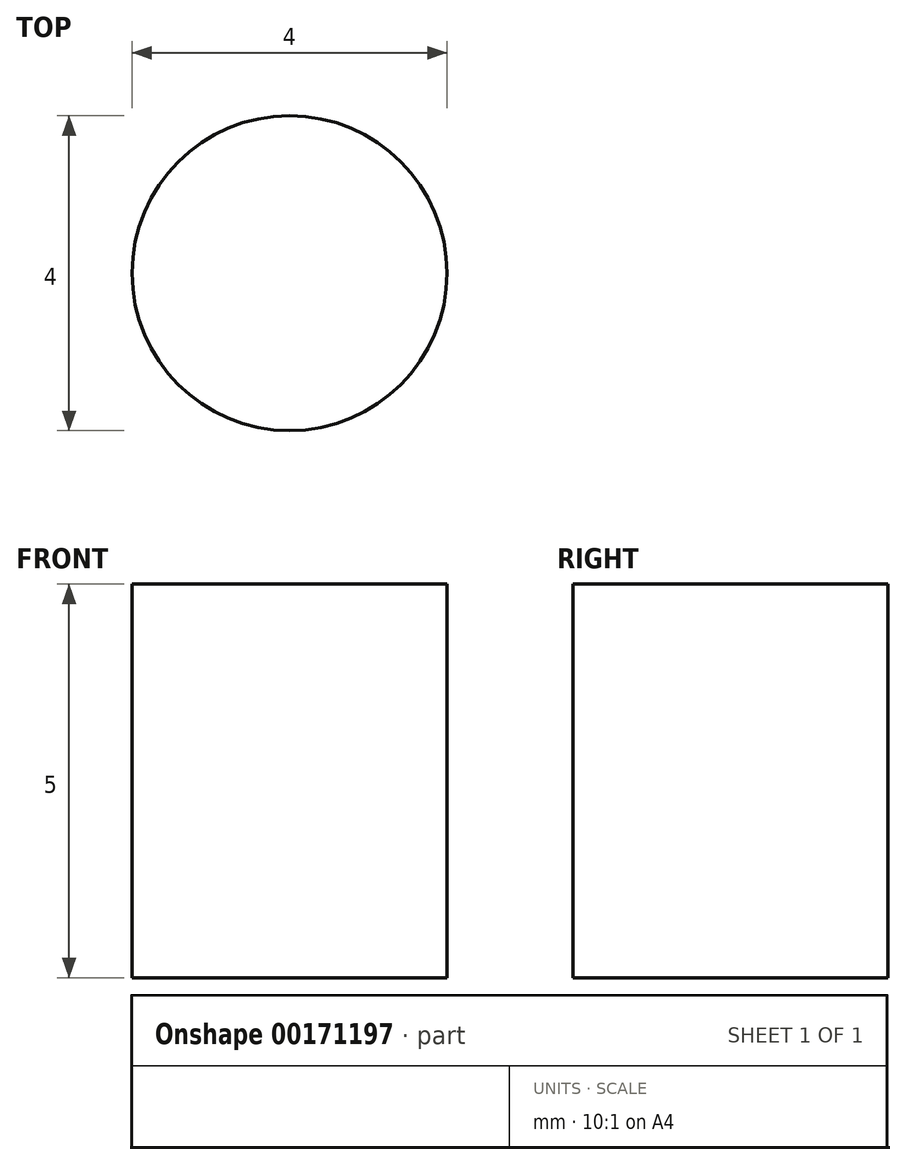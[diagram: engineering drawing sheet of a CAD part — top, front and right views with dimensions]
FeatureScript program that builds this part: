
annotation { "Feature Type Name" : "Feature", "Feature Type Description" : "" }
export const myFeature = defineFeature(function(context is Context, id is Id, definition is map)
    precondition{}
    {
        {
            var Q0;
            Q0=qCreatedBy(makeId("Top.planeOp"),FACE);
            var sketch = newSketch(context, id + "F0", { "sketchPlane" : qUnion([Q0])});
            skCircle(sketch, "E0", {"center": v(0, 0) * mm, "radius": 2 * mm});
            skLineSegment(sketch, "E1", {"start": v(5.33, 16.44) * mm, "end": v(4.24, 16.75) * mm});
            skArc(sketch, "E2", {"start": v(3.87, 17.95) * mm, "mid": v(3.86, 17.29) * mm, "end": v(4.24, 16.75) * mm});
            skArc(sketch, "E3", {"start": v(3.87, 17.95) * mm, "mid": v(3.9, 18.29) * mm, "end": v(3.9, 18.63) * mm});
            skLineSegment(sketch, "E4", {"start": v(3.9, 18.63) * mm, "end": v(3.86, 19) * mm});
            skArc(sketch, "E5", {"start": v(3.86, 19) * mm, "mid": v(3.65, 20.03) * mm, "end": v(3.31, 21.03) * mm});
            skLineSegment(sketch, "E6", {"start": v(3.31, 21.03) * mm, "end": v(3.26, 21.16) * mm});
            skLineSegment(sketch, "E7", {"start": v(3.26, 21.16) * mm, "end": v(2.02, 21.31) * mm});
            skLineSegment(sketch, "E8", {"start": v(2.02, 21.31) * mm, "end": v(1.93, 21.2) * mm});
            skArc(sketch, "E9", {"start": v(1.93, 21.2) * mm, "mid": v(1.37, 20.31) * mm, "end": v(0.91, 19.36) * mm});
            skLineSegment(sketch, "E10", {"start": v(0.91, 19.36) * mm, "end": v(0.79, 19.02) * mm});
            skArc(sketch, "E11", {"start": v(0.79, 19.02) * mm, "mid": v(0.69, 18.7) * mm, "end": v(0.64, 18.35) * mm});
            skArc(sketch, "E12", {"start": v(-0.01, 17.28) * mm, "mid": v(0.49, 17.7) * mm, "end": v(0.64, 18.35) * mm});
            skLineSegment(sketch, "E13", {"start": v(-0.01, 17.28) * mm, "end": v(-1.14, 17.24) * mm});
            skArc(sketch, "E14", {"start": v(-1.87, 18.27) * mm, "mid": v(-1.67, 17.64) * mm, "end": v(-1.14, 17.24) * mm});
            skArc(sketch, "E15", {"start": v(-1.87, 18.27) * mm, "mid": v(-1.93, 18.6) * mm, "end": v(-2.06, 18.92) * mm});
            skLineSegment(sketch, "E16", {"start": v(-2.06, 18.92) * mm, "end": v(-2.2, 19.26) * mm});
            skArc(sketch, "E17", {"start": v(-2.2, 19.26) * mm, "mid": v(-2.72, 20.18) * mm, "end": v(-3.35, 21.02) * mm});
            skLineSegment(sketch, "E18", {"start": v(-3.35, 21.02) * mm, "end": v(-3.44, 21.13) * mm});
            skLineSegment(sketch, "E19", {"start": v(-3.44, 21.13) * mm, "end": v(-4.67, 20.9) * mm});
            skLineSegment(sketch, "E20", {"start": v(-4.67, 20.9) * mm, "end": v(-4.71, 20.76) * mm});
            skArc(sketch, "E21", {"start": v(-4.71, 20.76) * mm, "mid": v(-4.98, 19.74) * mm, "end": v(-5.12, 18.7) * mm});
            skLineSegment(sketch, "E22", {"start": v(-5.12, 18.7) * mm, "end": v(-5.13, 18.33) * mm});
            skArc(sketch, "E23", {"start": v(-5.13, 18.33) * mm, "mid": v(-5.12, 17.99) * mm, "end": v(-5.06, 17.65) * mm});
            skArc(sketch, "E24", {"start": v(-5.35, 16.43) * mm, "mid": v(-5, 17) * mm, "end": v(-5.06, 17.65) * mm});
            skLineSegment(sketch, "E25", {"start": v(-5.35, 16.43) * mm, "end": v(-6.42, 16.04) * mm});
            skArc(sketch, "E26", {"start": v(-7.42, 16.8) * mm, "mid": v(-7.04, 16.26) * mm, "end": v(-6.42, 16.04) * mm});
            skArc(sketch, "E27", {"start": v(-7.42, 16.8) * mm, "mid": v(-7.59, 17.1) * mm, "end": v(-7.8, 17.36) * mm});
            skLineSegment(sketch, "E28", {"start": v(-7.8, 17.36) * mm, "end": v(-8.05, 17.64) * mm});
            skArc(sketch, "E29", {"start": v(-8.05, 17.64) * mm, "mid": v(-8.82, 18.35) * mm, "end": v(-9.68, 18.96) * mm});
            skLineSegment(sketch, "E30", {"start": v(-9.68, 18.96) * mm, "end": v(-9.8, 19.03) * mm});
            skLineSegment(sketch, "E31", {"start": v(-9.8, 19.03) * mm, "end": v(-10.9, 18.43) * mm});
            skLineSegment(sketch, "E32", {"start": v(-10.9, 18.43) * mm, "end": v(-10.9, 18.29) * mm});
            skArc(sketch, "E33", {"start": v(-10.9, 18.29) * mm, "mid": v(-10.83, 17.24) * mm, "end": v(-10.64, 16.2) * mm});
            skLineSegment(sketch, "E34", {"start": v(-10.64, 16.2) * mm, "end": v(-10.54, 15.85) * mm});
            skArc(sketch, "E35", {"start": v(-10.54, 15.85) * mm, "mid": v(-10.43, 15.52) * mm, "end": v(-10.27, 15.22) * mm});
            skArc(sketch, "E36", {"start": v(-10.16, 13.97) * mm, "mid": v(-10.01, 14.61) * mm, "end": v(-10.27, 15.22) * mm});
            skLineSegment(sketch, "E37", {"start": v(-10.16, 13.97) * mm, "end": v(-11.06, 13.27) * mm});
            skArc(sketch, "E38", {"start": v(-12.25, 13.68) * mm, "mid": v(-11.72, 13.28) * mm, "end": v(-11.06, 13.27) * mm});
            skArc(sketch, "E39", {"start": v(-12.25, 13.68) * mm, "mid": v(-12.5, 13.91) * mm, "end": v(-12.79, 14.1) * mm});
            skLineSegment(sketch, "E40", {"start": v(-12.79, 14.1) * mm, "end": v(-13.1, 14.29) * mm});
            skArc(sketch, "E41", {"start": v(-13.1, 14.29) * mm, "mid": v(-14.06, 14.72) * mm, "end": v(-15.06, 15.04) * mm});
            skLineSegment(sketch, "E42", {"start": v(-15.06, 15.04) * mm, "end": v(-15.2, 15.07) * mm});
            skLineSegment(sketch, "E43", {"start": v(-15.2, 15.07) * mm, "end": v(-16.06, 14.16) * mm});
            skLineSegment(sketch, "E44", {"start": v(-16.06, 14.16) * mm, "end": v(-16.01, 14.03) * mm});
            skArc(sketch, "E45", {"start": v(-16.01, 14.03) * mm, "mid": v(-15.63, 13.05) * mm, "end": v(-15.13, 12.12) * mm});
            skLineSegment(sketch, "E46", {"start": v(-15.13, 12.12) * mm, "end": v(-14.92, 11.82) * mm});
            skArc(sketch, "E47", {"start": v(-14.92, 11.82) * mm, "mid": v(-14.72, 11.54) * mm, "end": v(-14.47, 11.3) * mm});
            skArc(sketch, "E48", {"start": v(-13.98, 10.15) * mm, "mid": v(-14.04, 10.8) * mm, "end": v(-14.47, 11.3) * mm});
            skLineSegment(sketch, "E49", {"start": v(-13.98, 10.15) * mm, "end": v(-14.62, 9.2) * mm});
            skArc(sketch, "E50", {"start": v(-15.87, 9.23) * mm, "mid": v(-15.25, 9.01) * mm, "end": v(-14.62, 9.2) * mm});
            skArc(sketch, "E51", {"start": v(-15.87, 9.23) * mm, "mid": v(-16.19, 9.37) * mm, "end": v(-16.52, 9.46) * mm});
            skLineSegment(sketch, "E52", {"start": v(-16.52, 9.46) * mm, "end": v(-16.88, 9.54) * mm});
            skArc(sketch, "E53", {"start": v(-16.88, 9.54) * mm, "mid": v(-17.92, 9.66) * mm, "end": v(-18.97, 9.65) * mm});
            skLineSegment(sketch, "E54", {"start": v(-18.97, 9.65) * mm, "end": v(-19.12, 9.64) * mm});
            skLineSegment(sketch, "E55", {"start": v(-19.12, 9.64) * mm, "end": v(-19.65, 8.5) * mm});
            skLineSegment(sketch, "E56", {"start": v(-19.65, 8.5) * mm, "end": v(-19.56, 8.4) * mm});
            skArc(sketch, "E57", {"start": v(-19.56, 8.4) * mm, "mid": v(-18.9, 7.58) * mm, "end": v(-18.14, 6.85) * mm});
            skLineSegment(sketch, "E58", {"start": v(-18.14, 6.85) * mm, "end": v(-17.84, 6.63) * mm});
            skArc(sketch, "E59", {"start": v(-17.84, 6.63) * mm, "mid": v(-17.56, 6.43) * mm, "end": v(-17.25, 6.28) * mm});
            skArc(sketch, "E60", {"start": v(-16.44, 5.33) * mm, "mid": v(-16.69, 5.94) * mm, "end": v(-17.25, 6.28) * mm});
            skLineSegment(sketch, "E61", {"start": v(-16.44, 5.33) * mm, "end": v(-16.75, 4.24) * mm});
            skArc(sketch, "E62", {"start": v(-17.95, 3.87) * mm, "mid": v(-17.29, 3.86) * mm, "end": v(-16.75, 4.24) * mm});
            skArc(sketch, "E63", {"start": v(-17.95, 3.87) * mm, "mid": v(-18.29, 3.9) * mm, "end": v(-18.63, 3.9) * mm});
            skLineSegment(sketch, "E64", {"start": v(-18.63, 3.9) * mm, "end": v(-19, 3.86) * mm});
            skArc(sketch, "E65", {"start": v(-19, 3.86) * mm, "mid": v(-20.03, 3.65) * mm, "end": v(-21.03, 3.31) * mm});
            skLineSegment(sketch, "E66", {"start": v(-21.03, 3.31) * mm, "end": v(-21.16, 3.26) * mm});
            skLineSegment(sketch, "E67", {"start": v(-21.16, 3.26) * mm, "end": v(-21.31, 2.02) * mm});
            skLineSegment(sketch, "E68", {"start": v(-21.31, 2.02) * mm, "end": v(-21.2, 1.93) * mm});
            skArc(sketch, "E69", {"start": v(-21.2, 1.93) * mm, "mid": v(-20.31, 1.37) * mm, "end": v(-19.36, 0.91) * mm});
            skLineSegment(sketch, "E70", {"start": v(-19.36, 0.91) * mm, "end": v(-19.02, 0.79) * mm});
            skArc(sketch, "E71", {"start": v(-19.02, 0.79) * mm, "mid": v(-18.7, 0.69) * mm, "end": v(-18.35, 0.64) * mm});
            skArc(sketch, "E72", {"start": v(-17.28, -0.01) * mm, "mid": v(-17.7, 0.49) * mm, "end": v(-18.35, 0.64) * mm});
            skLineSegment(sketch, "E73", {"start": v(-17.28, -0.01) * mm, "end": v(-17.24, -1.14) * mm});
            skArc(sketch, "E74", {"start": v(-18.27, -1.87) * mm, "mid": v(-17.64, -1.67) * mm, "end": v(-17.24, -1.14) * mm});
            skArc(sketch, "E75", {"start": v(-18.27, -1.87) * mm, "mid": v(-18.6, -1.93) * mm, "end": v(-18.92, -2.06) * mm});
            skLineSegment(sketch, "E76", {"start": v(-18.92, -2.06) * mm, "end": v(-19.26, -2.2) * mm});
            skArc(sketch, "E77", {"start": v(-19.26, -2.2) * mm, "mid": v(-20.18, -2.72) * mm, "end": v(-21.02, -3.35) * mm});
            skLineSegment(sketch, "E78", {"start": v(-21.02, -3.35) * mm, "end": v(-21.13, -3.44) * mm});
            skLineSegment(sketch, "E79", {"start": v(-21.13, -3.44) * mm, "end": v(-20.9, -4.67) * mm});
            skLineSegment(sketch, "E80", {"start": v(-20.9, -4.67) * mm, "end": v(-20.76, -4.71) * mm});
            skArc(sketch, "E81", {"start": v(-20.76, -4.71) * mm, "mid": v(-19.74, -4.98) * mm, "end": v(-18.7, -5.12) * mm});
            skLineSegment(sketch, "E82", {"start": v(-18.7, -5.12) * mm, "end": v(-18.33, -5.13) * mm});
            skArc(sketch, "E83", {"start": v(-18.33, -5.13) * mm, "mid": v(-17.99, -5.12) * mm, "end": v(-17.65, -5.06) * mm});
            skArc(sketch, "E84", {"start": v(-16.43, -5.35) * mm, "mid": v(-17, -5) * mm, "end": v(-17.65, -5.06) * mm});
            skLineSegment(sketch, "E85", {"start": v(-16.43, -5.35) * mm, "end": v(-16.04, -6.42) * mm});
            skArc(sketch, "E86", {"start": v(-16.8, -7.42) * mm, "mid": v(-16.26, -7.04) * mm, "end": v(-16.04, -6.42) * mm});
            skArc(sketch, "E87", {"start": v(-16.8, -7.42) * mm, "mid": v(-17.1, -7.59) * mm, "end": v(-17.36, -7.8) * mm});
            skLineSegment(sketch, "E88", {"start": v(-17.36, -7.8) * mm, "end": v(-17.64, -8.05) * mm});
            skArc(sketch, "E89", {"start": v(-17.64, -8.05) * mm, "mid": v(-18.35, -8.82) * mm, "end": v(-18.96, -9.68) * mm});
            skLineSegment(sketch, "E90", {"start": v(-18.96, -9.68) * mm, "end": v(-19.03, -9.8) * mm});
            skLineSegment(sketch, "E91", {"start": v(-19.03, -9.8) * mm, "end": v(-18.43, -10.9) * mm});
            skLineSegment(sketch, "E92", {"start": v(-18.43, -10.9) * mm, "end": v(-18.29, -10.9) * mm});
            skArc(sketch, "E93", {"start": v(-18.29, -10.9) * mm, "mid": v(-17.24, -10.83) * mm, "end": v(-16.2, -10.64) * mm});
            skLineSegment(sketch, "E94", {"start": v(-16.2, -10.64) * mm, "end": v(-15.85, -10.54) * mm});
            skArc(sketch, "E95", {"start": v(-15.85, -10.54) * mm, "mid": v(-15.52, -10.43) * mm, "end": v(-15.22, -10.27) * mm});
            skArc(sketch, "E96", {"start": v(-13.97, -10.16) * mm, "mid": v(-14.61, -10.01) * mm, "end": v(-15.22, -10.27) * mm});
            skLineSegment(sketch, "E97", {"start": v(-13.97, -10.16) * mm, "end": v(-13.27, -11.06) * mm});
            skArc(sketch, "E98", {"start": v(-13.68, -12.25) * mm, "mid": v(-13.28, -11.72) * mm, "end": v(-13.27, -11.06) * mm});
            skArc(sketch, "E99", {"start": v(-13.68, -12.25) * mm, "mid": v(-13.91, -12.5) * mm, "end": v(-14.1, -12.79) * mm});
            skLineSegment(sketch, "E100", {"start": v(-14.1, -12.79) * mm, "end": v(-14.29, -13.1) * mm});
            skArc(sketch, "E101", {"start": v(-14.29, -13.1) * mm, "mid": v(-14.72, -14.06) * mm, "end": v(-15.04, -15.06) * mm});
            skLineSegment(sketch, "E102", {"start": v(-15.04, -15.06) * mm, "end": v(-15.07, -15.2) * mm});
            skLineSegment(sketch, "E103", {"start": v(-15.07, -15.2) * mm, "end": v(-14.16, -16.06) * mm});
            skLineSegment(sketch, "E104", {"start": v(-14.16, -16.06) * mm, "end": v(-14.03, -16.01) * mm});
            skArc(sketch, "E105", {"start": v(-14.03, -16.01) * mm, "mid": v(-13.05, -15.63) * mm, "end": v(-12.12, -15.13) * mm});
            skLineSegment(sketch, "E106", {"start": v(-12.12, -15.13) * mm, "end": v(-11.82, -14.92) * mm});
            skArc(sketch, "E107", {"start": v(-11.82, -14.92) * mm, "mid": v(-11.54, -14.72) * mm, "end": v(-11.3, -14.47) * mm});
            skArc(sketch, "E108", {"start": v(-10.15, -13.98) * mm, "mid": v(-10.8, -14.04) * mm, "end": v(-11.3, -14.47) * mm});
            skLineSegment(sketch, "E109", {"start": v(-10.15, -13.98) * mm, "end": v(-9.2, -14.62) * mm});
            skArc(sketch, "E110", {"start": v(-9.23, -15.87) * mm, "mid": v(-9.01, -15.25) * mm, "end": v(-9.2, -14.62) * mm});
            skArc(sketch, "E111", {"start": v(-9.23, -15.87) * mm, "mid": v(-9.37, -16.19) * mm, "end": v(-9.46, -16.52) * mm});
            skLineSegment(sketch, "E112", {"start": v(-9.46, -16.52) * mm, "end": v(-9.54, -16.88) * mm});
            skArc(sketch, "E113", {"start": v(-9.54, -16.88) * mm, "mid": v(-9.66, -17.92) * mm, "end": v(-9.65, -18.97) * mm});
            skLineSegment(sketch, "E114", {"start": v(-9.65, -18.97) * mm, "end": v(-9.64, -19.12) * mm});
            skLineSegment(sketch, "E115", {"start": v(-9.64, -19.12) * mm, "end": v(-8.5, -19.65) * mm});
            skLineSegment(sketch, "E116", {"start": v(-8.5, -19.65) * mm, "end": v(-8.4, -19.56) * mm});
            skArc(sketch, "E117", {"start": v(-8.4, -19.56) * mm, "mid": v(-7.58, -18.9) * mm, "end": v(-6.85, -18.14) * mm});
            skLineSegment(sketch, "E118", {"start": v(-6.85, -18.14) * mm, "end": v(-6.63, -17.84) * mm});
            skArc(sketch, "E119", {"start": v(-6.63, -17.84) * mm, "mid": v(-6.43, -17.56) * mm, "end": v(-6.28, -17.25) * mm});
            skArc(sketch, "E120", {"start": v(-5.33, -16.44) * mm, "mid": v(-5.94, -16.69) * mm, "end": v(-6.28, -17.25) * mm});
            skLineSegment(sketch, "E121", {"start": v(-5.33, -16.44) * mm, "end": v(-4.24, -16.75) * mm});
            skArc(sketch, "E122", {"start": v(-3.87, -17.95) * mm, "mid": v(-3.86, -17.29) * mm, "end": v(-4.24, -16.75) * mm});
            skArc(sketch, "E123", {"start": v(-3.87, -17.95) * mm, "mid": v(-3.9, -18.29) * mm, "end": v(-3.9, -18.63) * mm});
            skLineSegment(sketch, "E124", {"start": v(-3.9, -18.63) * mm, "end": v(-3.86, -19) * mm});
            skArc(sketch, "E125", {"start": v(-3.86, -19) * mm, "mid": v(-3.65, -20.03) * mm, "end": v(-3.31, -21.03) * mm});
            skLineSegment(sketch, "E126", {"start": v(-3.31, -21.03) * mm, "end": v(-3.26, -21.16) * mm});
            skLineSegment(sketch, "E127", {"start": v(-3.26, -21.16) * mm, "end": v(-2.02, -21.31) * mm});
            skLineSegment(sketch, "E128", {"start": v(-2.02, -21.31) * mm, "end": v(-1.93, -21.2) * mm});
            skArc(sketch, "E129", {"start": v(-1.93, -21.2) * mm, "mid": v(-1.37, -20.31) * mm, "end": v(-0.91, -19.36) * mm});
            skLineSegment(sketch, "E130", {"start": v(-0.91, -19.36) * mm, "end": v(-0.79, -19.02) * mm});
            skArc(sketch, "E131", {"start": v(-0.79, -19.02) * mm, "mid": v(-0.69, -18.7) * mm, "end": v(-0.64, -18.35) * mm});
            skArc(sketch, "E132", {"start": v(0.01, -17.28) * mm, "mid": v(-0.49, -17.7) * mm, "end": v(-0.64, -18.35) * mm});
            skLineSegment(sketch, "E133", {"start": v(0.01, -17.28) * mm, "end": v(1.14, -17.24) * mm});
            skArc(sketch, "E134", {"start": v(1.87, -18.27) * mm, "mid": v(1.67, -17.64) * mm, "end": v(1.14, -17.24) * mm});
            skArc(sketch, "E135", {"start": v(1.87, -18.27) * mm, "mid": v(1.93, -18.6) * mm, "end": v(2.06, -18.92) * mm});
            skLineSegment(sketch, "E136", {"start": v(2.06, -18.92) * mm, "end": v(2.2, -19.26) * mm});
            skArc(sketch, "E137", {"start": v(2.2, -19.26) * mm, "mid": v(2.72, -20.18) * mm, "end": v(3.35, -21.02) * mm});
            skLineSegment(sketch, "E138", {"start": v(3.35, -21.02) * mm, "end": v(3.44, -21.13) * mm});
            skLineSegment(sketch, "E139", {"start": v(3.44, -21.13) * mm, "end": v(4.67, -20.9) * mm});
            skLineSegment(sketch, "E140", {"start": v(4.67, -20.9) * mm, "end": v(4.71, -20.76) * mm});
            skArc(sketch, "E141", {"start": v(4.71, -20.76) * mm, "mid": v(4.98, -19.74) * mm, "end": v(5.12, -18.7) * mm});
            skLineSegment(sketch, "E142", {"start": v(5.12, -18.7) * mm, "end": v(5.13, -18.33) * mm});
            skArc(sketch, "E143", {"start": v(5.13, -18.33) * mm, "mid": v(5.12, -17.99) * mm, "end": v(5.06, -17.65) * mm});
            skArc(sketch, "E144", {"start": v(5.35, -16.43) * mm, "mid": v(5, -17) * mm, "end": v(5.06, -17.65) * mm});
            skLineSegment(sketch, "E145", {"start": v(5.35, -16.43) * mm, "end": v(6.42, -16.04) * mm});
            skArc(sketch, "E146", {"start": v(7.42, -16.8) * mm, "mid": v(7.04, -16.26) * mm, "end": v(6.42, -16.04) * mm});
            skArc(sketch, "E147", {"start": v(7.42, -16.8) * mm, "mid": v(7.59, -17.1) * mm, "end": v(7.8, -17.36) * mm});
            skLineSegment(sketch, "E148", {"start": v(7.8, -17.36) * mm, "end": v(8.05, -17.64) * mm});
            skArc(sketch, "E149", {"start": v(8.05, -17.64) * mm, "mid": v(8.82, -18.35) * mm, "end": v(9.68, -18.96) * mm});
            skLineSegment(sketch, "E150", {"start": v(9.68, -18.96) * mm, "end": v(9.8, -19.03) * mm});
            skLineSegment(sketch, "E151", {"start": v(9.8, -19.03) * mm, "end": v(10.9, -18.43) * mm});
            skLineSegment(sketch, "E152", {"start": v(10.9, -18.43) * mm, "end": v(10.9, -18.29) * mm});
            skArc(sketch, "E153", {"start": v(10.9, -18.29) * mm, "mid": v(10.83, -17.24) * mm, "end": v(10.64, -16.2) * mm});
            skLineSegment(sketch, "E154", {"start": v(10.64, -16.2) * mm, "end": v(10.54, -15.85) * mm});
            skArc(sketch, "E155", {"start": v(10.54, -15.85) * mm, "mid": v(10.43, -15.52) * mm, "end": v(10.27, -15.22) * mm});
            skArc(sketch, "E156", {"start": v(10.16, -13.97) * mm, "mid": v(10.01, -14.61) * mm, "end": v(10.27, -15.22) * mm});
            skLineSegment(sketch, "E157", {"start": v(10.16, -13.97) * mm, "end": v(11.06, -13.27) * mm});
            skArc(sketch, "E158", {"start": v(12.25, -13.68) * mm, "mid": v(11.72, -13.28) * mm, "end": v(11.06, -13.27) * mm});
            skArc(sketch, "E159", {"start": v(12.25, -13.68) * mm, "mid": v(12.5, -13.91) * mm, "end": v(12.79, -14.1) * mm});
            skLineSegment(sketch, "E160", {"start": v(12.79, -14.1) * mm, "end": v(13.1, -14.29) * mm});
            skArc(sketch, "E161", {"start": v(13.1, -14.29) * mm, "mid": v(14.06, -14.72) * mm, "end": v(15.06, -15.04) * mm});
            skLineSegment(sketch, "E162", {"start": v(15.06, -15.04) * mm, "end": v(15.2, -15.07) * mm});
            skLineSegment(sketch, "E163", {"start": v(15.2, -15.07) * mm, "end": v(16.06, -14.16) * mm});
            skLineSegment(sketch, "E164", {"start": v(16.06, -14.16) * mm, "end": v(16.01, -14.03) * mm});
            skArc(sketch, "E165", {"start": v(16.01, -14.03) * mm, "mid": v(15.63, -13.05) * mm, "end": v(15.13, -12.12) * mm});
            skLineSegment(sketch, "E166", {"start": v(15.13, -12.12) * mm, "end": v(14.92, -11.82) * mm});
            skArc(sketch, "E167", {"start": v(14.92, -11.82) * mm, "mid": v(14.72, -11.54) * mm, "end": v(14.47, -11.3) * mm});
            skArc(sketch, "E168", {"start": v(13.98, -10.15) * mm, "mid": v(14.04, -10.8) * mm, "end": v(14.47, -11.3) * mm});
            skLineSegment(sketch, "E169", {"start": v(13.98, -10.15) * mm, "end": v(14.62, -9.2) * mm});
            skArc(sketch, "E170", {"start": v(15.87, -9.23) * mm, "mid": v(15.25, -9.01) * mm, "end": v(14.62, -9.2) * mm});
            skArc(sketch, "E171", {"start": v(15.87, -9.23) * mm, "mid": v(16.19, -9.37) * mm, "end": v(16.52, -9.46) * mm});
            skLineSegment(sketch, "E172", {"start": v(16.52, -9.46) * mm, "end": v(16.88, -9.54) * mm});
            skArc(sketch, "E173", {"start": v(16.88, -9.54) * mm, "mid": v(17.92, -9.66) * mm, "end": v(18.97, -9.65) * mm});
            skLineSegment(sketch, "E174", {"start": v(18.97, -9.65) * mm, "end": v(19.12, -9.64) * mm});
            skLineSegment(sketch, "E175", {"start": v(19.12, -9.64) * mm, "end": v(19.65, -8.5) * mm});
            skLineSegment(sketch, "E176", {"start": v(19.65, -8.5) * mm, "end": v(19.56, -8.4) * mm});
            skArc(sketch, "E177", {"start": v(19.56, -8.4) * mm, "mid": v(18.9, -7.58) * mm, "end": v(18.14, -6.85) * mm});
            skLineSegment(sketch, "E178", {"start": v(18.14, -6.85) * mm, "end": v(17.84, -6.63) * mm});
            skArc(sketch, "E179", {"start": v(17.84, -6.63) * mm, "mid": v(17.56, -6.43) * mm, "end": v(17.25, -6.28) * mm});
            skArc(sketch, "E180", {"start": v(16.44, -5.33) * mm, "mid": v(16.69, -5.94) * mm, "end": v(17.25, -6.28) * mm});
            skLineSegment(sketch, "E181", {"start": v(16.44, -5.33) * mm, "end": v(16.75, -4.24) * mm});
            skArc(sketch, "E182", {"start": v(17.95, -3.87) * mm, "mid": v(17.29, -3.86) * mm, "end": v(16.75, -4.24) * mm});
            skArc(sketch, "E183", {"start": v(17.95, -3.87) * mm, "mid": v(18.29, -3.9) * mm, "end": v(18.63, -3.9) * mm});
            skLineSegment(sketch, "E184", {"start": v(18.63, -3.9) * mm, "end": v(19, -3.86) * mm});
            skArc(sketch, "E185", {"start": v(19, -3.86) * mm, "mid": v(20.03, -3.65) * mm, "end": v(21.03, -3.31) * mm});
            skLineSegment(sketch, "E186", {"start": v(21.03, -3.31) * mm, "end": v(21.16, -3.26) * mm});
            skLineSegment(sketch, "E187", {"start": v(21.16, -3.26) * mm, "end": v(21.31, -2.02) * mm});
            skLineSegment(sketch, "E188", {"start": v(21.31, -2.02) * mm, "end": v(21.2, -1.93) * mm});
            skArc(sketch, "E189", {"start": v(21.2, -1.93) * mm, "mid": v(20.31, -1.37) * mm, "end": v(19.36, -0.91) * mm});
            skLineSegment(sketch, "E190", {"start": v(19.36, -0.91) * mm, "end": v(19.02, -0.79) * mm});
            skArc(sketch, "E191", {"start": v(19.02, -0.79) * mm, "mid": v(18.7, -0.69) * mm, "end": v(18.35, -0.64) * mm});
            skArc(sketch, "E192", {"start": v(17.28, 0.01) * mm, "mid": v(17.7, -0.49) * mm, "end": v(18.35, -0.64) * mm});
            skLineSegment(sketch, "E193", {"start": v(17.28, 0.01) * mm, "end": v(17.24, 1.14) * mm});
            skArc(sketch, "E194", {"start": v(18.27, 1.87) * mm, "mid": v(17.64, 1.67) * mm, "end": v(17.24, 1.14) * mm});
            skArc(sketch, "E195", {"start": v(18.27, 1.87) * mm, "mid": v(18.6, 1.93) * mm, "end": v(18.92, 2.06) * mm});
            skLineSegment(sketch, "E196", {"start": v(18.92, 2.06) * mm, "end": v(19.26, 2.2) * mm});
            skArc(sketch, "E197", {"start": v(19.26, 2.2) * mm, "mid": v(20.18, 2.72) * mm, "end": v(21.02, 3.35) * mm});
            skLineSegment(sketch, "E198", {"start": v(21.02, 3.35) * mm, "end": v(21.13, 3.44) * mm});
            skLineSegment(sketch, "E199", {"start": v(21.13, 3.44) * mm, "end": v(20.9, 4.67) * mm});
            skLineSegment(sketch, "E200", {"start": v(20.9, 4.67) * mm, "end": v(20.76, 4.71) * mm});
            skArc(sketch, "E201", {"start": v(20.76, 4.71) * mm, "mid": v(19.74, 4.98) * mm, "end": v(18.7, 5.12) * mm});
            skLineSegment(sketch, "E202", {"start": v(18.7, 5.12) * mm, "end": v(18.33, 5.13) * mm});
            skArc(sketch, "E203", {"start": v(18.33, 5.13) * mm, "mid": v(17.99, 5.12) * mm, "end": v(17.65, 5.06) * mm});
            skArc(sketch, "E204", {"start": v(16.43, 5.35) * mm, "mid": v(17, 5) * mm, "end": v(17.65, 5.06) * mm});
            skLineSegment(sketch, "E205", {"start": v(16.43, 5.35) * mm, "end": v(16.04, 6.42) * mm});
            skArc(sketch, "E206", {"start": v(16.8, 7.42) * mm, "mid": v(16.26, 7.04) * mm, "end": v(16.04, 6.42) * mm});
            skArc(sketch, "E207", {"start": v(16.8, 7.42) * mm, "mid": v(17.1, 7.59) * mm, "end": v(17.36, 7.8) * mm});
            skLineSegment(sketch, "E208", {"start": v(17.36, 7.8) * mm, "end": v(17.64, 8.05) * mm});
            skArc(sketch, "E209", {"start": v(17.64, 8.05) * mm, "mid": v(18.35, 8.82) * mm, "end": v(18.96, 9.68) * mm});
            skLineSegment(sketch, "E210", {"start": v(18.96, 9.68) * mm, "end": v(19.03, 9.8) * mm});
            skLineSegment(sketch, "E211", {"start": v(19.03, 9.8) * mm, "end": v(18.43, 10.9) * mm});
            skLineSegment(sketch, "E212", {"start": v(18.43, 10.9) * mm, "end": v(18.29, 10.9) * mm});
            skArc(sketch, "E213", {"start": v(18.29, 10.9) * mm, "mid": v(17.24, 10.83) * mm, "end": v(16.2, 10.64) * mm});
            skLineSegment(sketch, "E214", {"start": v(16.2, 10.64) * mm, "end": v(15.85, 10.54) * mm});
            skArc(sketch, "E215", {"start": v(15.85, 10.54) * mm, "mid": v(15.52, 10.43) * mm, "end": v(15.22, 10.27) * mm});
            skArc(sketch, "E216", {"start": v(13.97, 10.16) * mm, "mid": v(14.61, 10.01) * mm, "end": v(15.22, 10.27) * mm});
            skLineSegment(sketch, "E217", {"start": v(13.97, 10.16) * mm, "end": v(13.27, 11.06) * mm});
            skArc(sketch, "E218", {"start": v(13.68, 12.25) * mm, "mid": v(13.28, 11.72) * mm, "end": v(13.27, 11.06) * mm});
            skArc(sketch, "E219", {"start": v(13.68, 12.25) * mm, "mid": v(13.91, 12.5) * mm, "end": v(14.1, 12.79) * mm});
            skLineSegment(sketch, "E220", {"start": v(14.1, 12.79) * mm, "end": v(14.29, 13.1) * mm});
            skArc(sketch, "E221", {"start": v(14.29, 13.1) * mm, "mid": v(14.72, 14.06) * mm, "end": v(15.04, 15.06) * mm});
            skLineSegment(sketch, "E222", {"start": v(15.04, 15.06) * mm, "end": v(15.07, 15.2) * mm});
            skLineSegment(sketch, "E223", {"start": v(15.07, 15.2) * mm, "end": v(14.16, 16.06) * mm});
            skLineSegment(sketch, "E224", {"start": v(14.16, 16.06) * mm, "end": v(14.03, 16.01) * mm});
            skArc(sketch, "E225", {"start": v(14.03, 16.01) * mm, "mid": v(13.05, 15.63) * mm, "end": v(12.12, 15.13) * mm});
            skLineSegment(sketch, "E226", {"start": v(12.12, 15.13) * mm, "end": v(11.82, 14.92) * mm});
            skArc(sketch, "E227", {"start": v(11.82, 14.92) * mm, "mid": v(11.54, 14.72) * mm, "end": v(11.3, 14.47) * mm});
            skArc(sketch, "E228", {"start": v(10.15, 13.98) * mm, "mid": v(10.8, 14.04) * mm, "end": v(11.3, 14.47) * mm});
            skLineSegment(sketch, "E229", {"start": v(10.15, 13.98) * mm, "end": v(9.2, 14.62) * mm});
            skArc(sketch, "E230", {"start": v(9.23, 15.87) * mm, "mid": v(9.01, 15.25) * mm, "end": v(9.2, 14.62) * mm});
            skArc(sketch, "E231", {"start": v(9.23, 15.87) * mm, "mid": v(9.37, 16.19) * mm, "end": v(9.46, 16.52) * mm});
            skLineSegment(sketch, "E232", {"start": v(9.46, 16.52) * mm, "end": v(9.54, 16.88) * mm});
            skArc(sketch, "E233", {"start": v(9.54, 16.88) * mm, "mid": v(9.66, 17.92) * mm, "end": v(9.65, 18.97) * mm});
            skLineSegment(sketch, "E234", {"start": v(9.65, 18.97) * mm, "end": v(9.64, 19.12) * mm});
            skLineSegment(sketch, "E235", {"start": v(9.64, 19.12) * mm, "end": v(8.5, 19.65) * mm});
            skLineSegment(sketch, "E236", {"start": v(8.5, 19.65) * mm, "end": v(8.4, 19.56) * mm});
            skArc(sketch, "E237", {"start": v(8.4, 19.56) * mm, "mid": v(7.58, 18.9) * mm, "end": v(6.85, 18.14) * mm});
            skLineSegment(sketch, "E238", {"start": v(6.85, 18.14) * mm, "end": v(6.63, 17.84) * mm});
            skArc(sketch, "E239", {"start": v(6.63, 17.84) * mm, "mid": v(6.43, 17.56) * mm, "end": v(6.28, 17.25) * mm});
            skArc(sketch, "E240", {"start": v(5.33, 16.44) * mm, "mid": v(5.94, 16.69) * mm, "end": v(6.28, 17.25) * mm});
            skSolve(sketch);
        }
        {
            var Q0;
            Q0=makeQuery(id+"F0.imprint","IMPRINT",FACE,{"disambiguationData":[TD([[makeQuery(id+"F0.imprint","IMPRINT",EDGE,{"derivedFrom":sQuery(id+"F0.wireOp",EDGE,"E0")}),1.0]])]});
            extrude(context, id + "F1", {"entities" : qUnion([Q0]), "depth" : 5 * mm});
        }
    });
